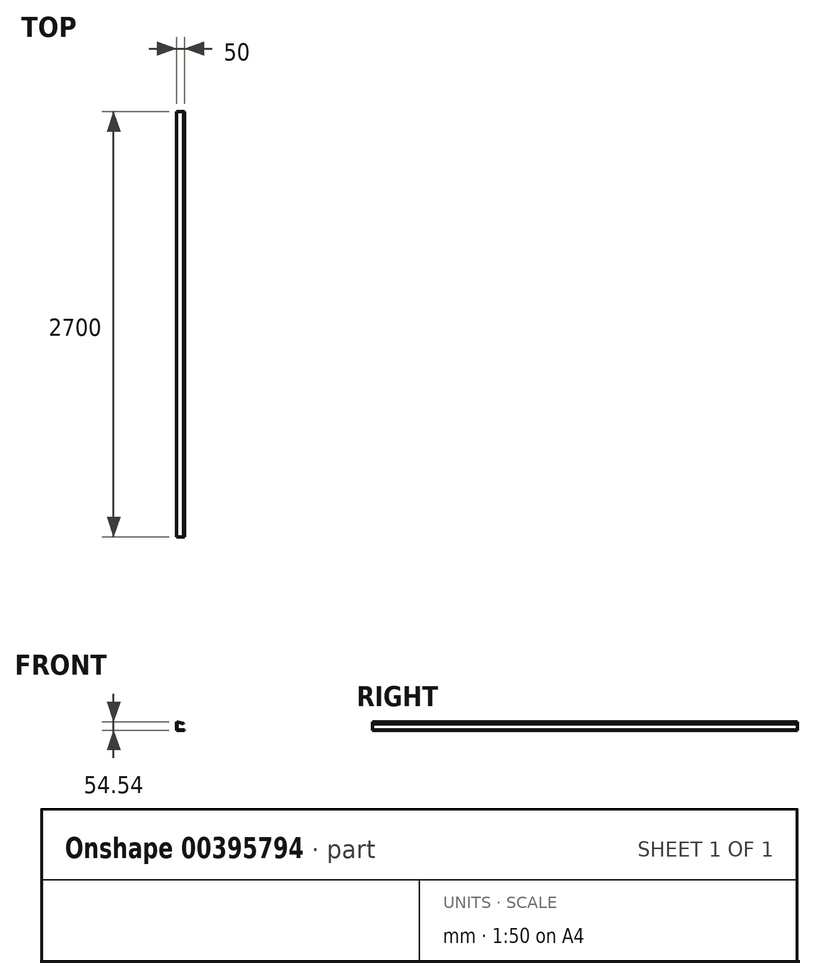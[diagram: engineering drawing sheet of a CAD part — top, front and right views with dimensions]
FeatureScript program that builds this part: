
annotation { "Feature Type Name" : "Feature", "Feature Type Description" : "" }
export const myFeature = defineFeature(function(context is Context, id is Id, definition is map)
    precondition{}
    {
        {
            var Q0;
            Q0=qCreatedBy(makeId("Front.planeOp"),FACE);
            var sketch = newSketch(context, id + "F0", { "sketchPlane" : qUnion([Q0])});
            skLineSegment(sketch, "E0", {"start": v(0, 0) * mm, "end": v(50, 0) * mm});
            skLineSegment(sketch, "E1", {"start": v(50, 0) * mm, "end": v(50, 2) * mm});
            skLineSegment(sketch, "E2", {"start": v(50, 2) * mm, "end": v(42, 2) * mm});
            skLineSegment(sketch, "E3", {"start": v(42, 2) * mm, "end": v(2, 2) * mm});
            skLineSegment(sketch, "E4", {"start": v(2, 2) * mm, "end": v(2, 52) * mm});
            skLineSegment(sketch, "E5", {"start": v(2, 52) * mm, "end": v(42.6, 42.17) * mm});
            skLineSegment(sketch, "E6", {"start": v(42.6, 42.17) * mm, "end": v(43.06, 44.11) * mm});
            skLineSegment(sketch, "E7", {"start": v(43.06, 44.11) * mm, "end": v(0, 54.54) * mm});
            skLineSegment(sketch, "E8", {"start": v(0, 54.54) * mm, "end": v(0, 0) * mm});
            skSolve(sketch);
        }
        {
            var Q0;
            Q0 = qSketchRegion(id + "F0", true);
            extrude(context, id + "F1", {"entities" : qUnion([Q0]), "depth" : 2700 * mm, "offsetDistance" : 25 * mm});
        }
    });
